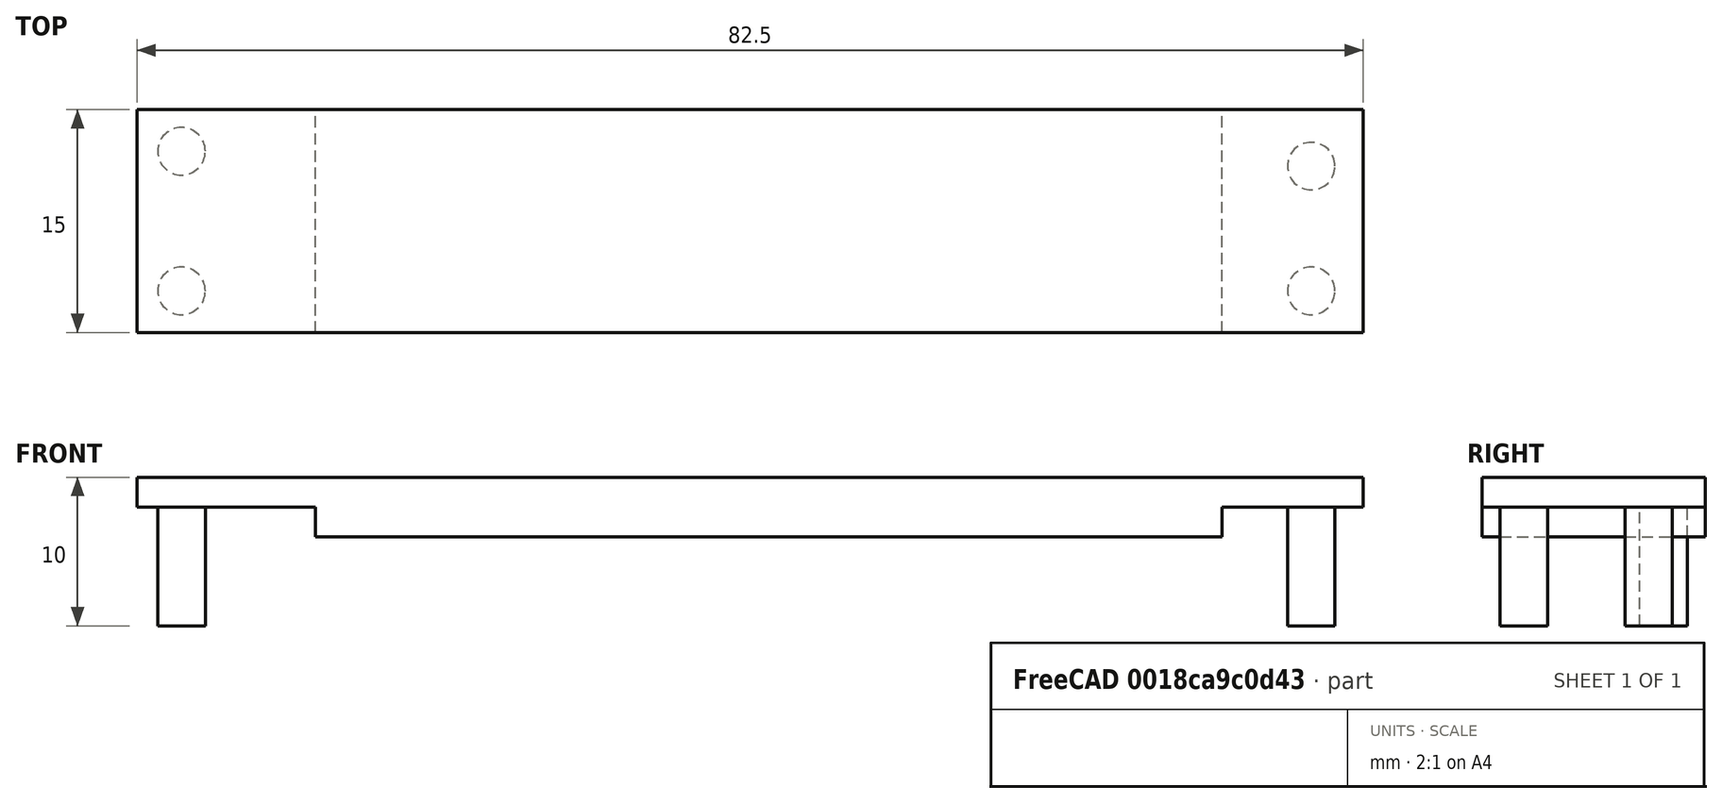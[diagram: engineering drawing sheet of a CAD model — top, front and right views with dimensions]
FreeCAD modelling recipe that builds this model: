
FCSTD DOCUMENT  (FreeCAD 0.17R13522 (Git))
Label: perforador_display_7segments
License: All rights reserved
LicenseURL: http://en.wikipedia.org/wiki/All_rights_reserved
objects: Part::Fuse×9, Part::Cylinder×4, Part::Box×2, Part::Feature×2
note: 17 computed .brp shape members not serialized (recipe doc carries the construction recipe); baked Part::Feature solids carry a one-line shape summary decoded from their .brp

FEATURE [Part::Box] Box  label="base_grande"
  AttacherType = Attacher::AttachEngine3D
  Height = 2
  Length = 82.5
  Width = 15
FEATURE [Part::Box] Box001  label="perfora_2mm_centro"
  AttacherType = Attacher::AttachEngine3D
  Height = 2
  Length = 61
  Placement = pos=(12,0,-2) rot=(0,0,1;0rad)
  Width = 15
FEATURE [Part::Fuse] Fusion
  Base = -> Box
  Placement = pos=(-3,-11,-2) rot=(0,0,1;0rad)
  Tool = -> Box001
FEATURE [Part::Cylinder] Cylinder  label="taladro1"
  Angle = 360
  AttacherType = Attacher::AttachEngine3D
  Height = 10
  Placement = pos=(0,1.2,-10) rot=(0,0,1;0rad)
  Radius = 1.6
FEATURE [Part::Cylinder] Cylinder001  label="taladro2"
  Angle = 360
  AttacherType = Attacher::AttachEngine3D
  Height = 10
  Placement = pos=(0,-8.2,-10) rot=(0,0,1;0rad)
  Radius = 1.6
FEATURE [Part::Cylinder] Cylinder002  label="taladro3"
  Angle = 360
  AttacherType = Attacher::AttachEngine3D
  Height = 10
  Placement = pos=(76,-8.2,-10) rot=(0,0,1;0rad)
  Radius = 1.6
FEATURE [Part::Cylinder] Cylinder003  label="taladro4"
  Angle = 360
  AttacherType = Attacher::AttachEngine3D
  Height = 10
  Placement = pos=(76,0.2,-10) rot=(0,0,1;0rad)
  Radius = 1.6
FEATURE [Part::Fuse] Fusion001
  Base = -> Fusion
  Tool = -> Cylinder
FEATURE [Part::Fuse] Fusion002
  Base = -> Cylinder003
  Tool = -> Fusion001
FEATURE [Part::Fuse] Fusion003
  Base = -> Cylinder002
  Tool = -> Fusion002
FEATURE [Part::Fuse] Fusion004
  Base = -> Cylinder001
  Tool = -> Fusion003
FEATURE [Part::Fuse] Fusion005
  Base = -> Cylinder
  Refine = true
  Tool = -> Fusion001
FEATURE [Part::Fuse] Fusion006
  Base = -> Cylinder003
  Refine = true
  Tool = -> Fusion001
FEATURE [Part::Fuse] Fusion007
  Base = -> Cylinder002
  Refine = true
  Tool = -> Fusion002
FEATURE [Part::Fuse] Fusion008
  Base = -> Cylinder001
  Refine = true
  Tool = -> Fusion003
FEATURE [Part::Feature] Fusion008_solid  label="Fusion008 (Solid)"
  shape: bbox 82.5 x 15 x 10 mm, 18 faces (baked)
FEATURE [Part::Feature] Fusion008001  label="Fusion009"
  shape: bbox 82.5 x 15 x 10 mm, 18 faces (baked)
